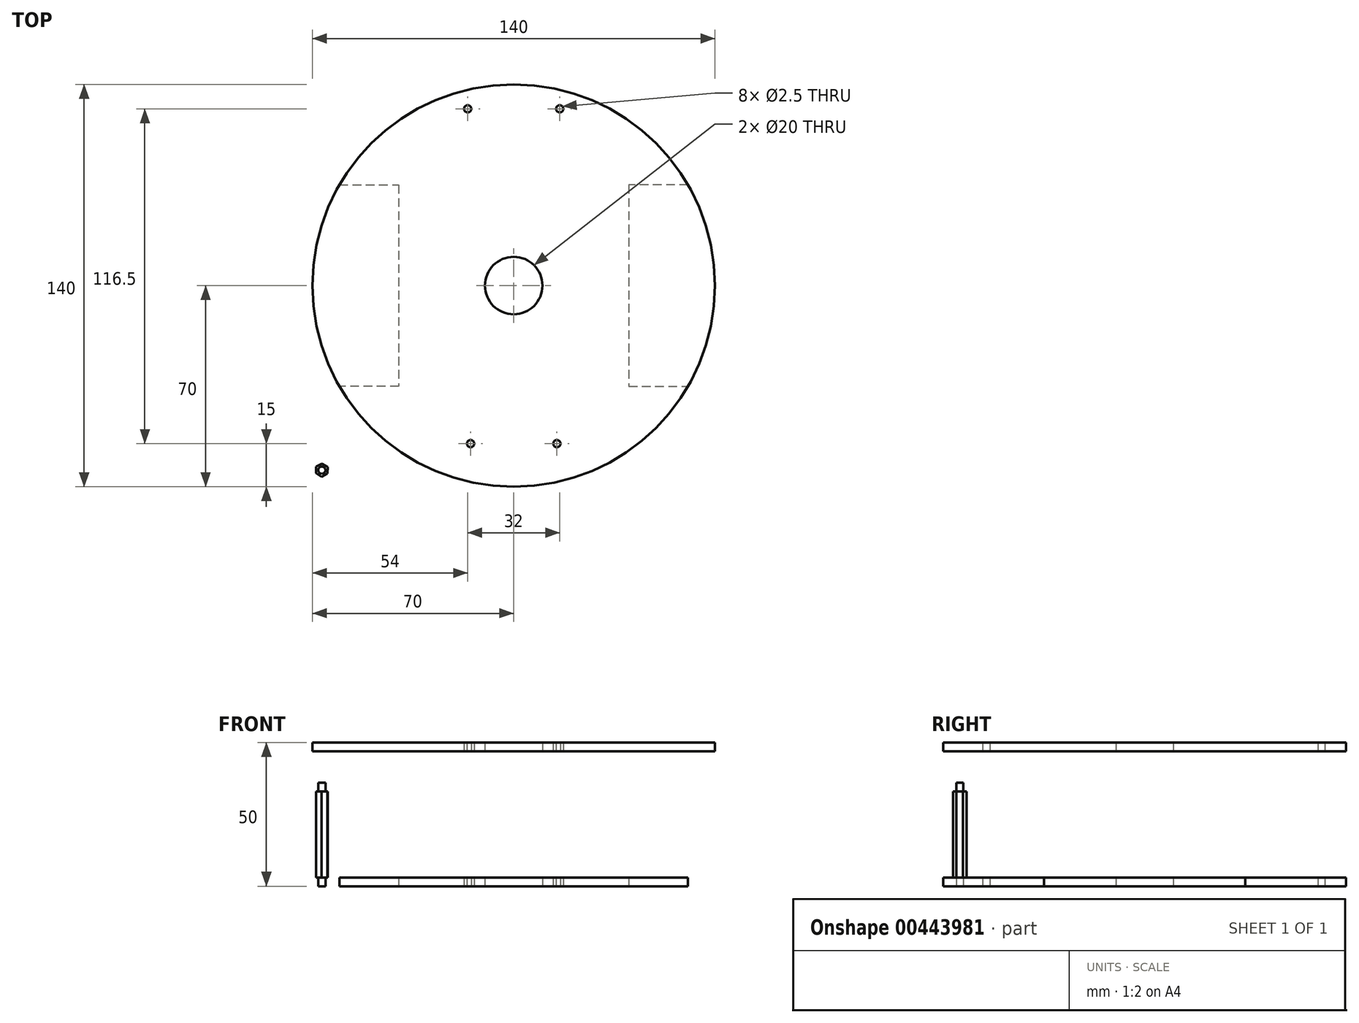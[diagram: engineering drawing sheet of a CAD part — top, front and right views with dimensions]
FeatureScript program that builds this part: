
annotation { "Feature Type Name" : "Feature", "Feature Type Description" : "" }
export const myFeature = defineFeature(function(context is Context, id is Id, definition is map)
    precondition{}
    {
        {
            var Q0;
            Q0=qCreatedBy(makeId("Top.planeOp"),FACE);
            var sketch = newSketch(context, id + "F0", { "sketchPlane" : qUnion([Q0])});
            skCircle(sketch, "E0", {"center": v(0, 0) * mm, "radius": 70 * mm});
            skCircle(sketch, "E1", {"center": v(0, 0) * mm, "radius": 10 * mm});
            skLineSegment(sketch, "E2", {"start": v(-88.17, 35) * mm, "end": v(88.24, 35) * mm, "construction": true});
            skLineSegment(sketch, "E3", {"start": v(88.24, 35) * mm, "end": v(88.24, -35) * mm, "construction": true});
            skLineSegment(sketch, "E4", {"start": v(88.24, -35) * mm, "end": v(-103.41, -35) * mm, "construction": true});
            skLineSegment(sketch, "E5", {"start": v(40, 80.8) * mm, "end": v(40, -81.17) * mm, "construction": true});
            skLineSegment(sketch, "E6", {"start": v(40, -81.17) * mm, "end": v(-40, -81.17) * mm, "construction": true});
            skLineSegment(sketch, "E7", {"start": v(-40, -81.17) * mm, "end": v(-40, 80.41) * mm, "construction": true});
            skLineSegment(sketch, "E8", {"start": v(60.62, 35) * mm, "end": v(40, 35) * mm});
            skLineSegment(sketch, "E9", {"start": v(40, 35) * mm, "end": v(40, -35) * mm});
            skLineSegment(sketch, "E10", {"start": v(40, -35) * mm, "end": v(60.62, -35) * mm});
            skLineSegment(sketch, "E11", {"start": v(-60.62, 35) * mm, "end": v(-40, 35) * mm});
            skLineSegment(sketch, "E12", {"start": v(-40, 35) * mm, "end": v(-40, -35) * mm});
            skLineSegment(sketch, "E13", {"start": v(-40, -35) * mm, "end": v(-60.62, -35) * mm});
            skLineSegment(sketch, "E14", {"start": v(-55.36, 61.5) * mm, "end": v(61.88, 61.5) * mm, "construction": true});
            skLineSegment(sketch, "E15", {"start": v(-62.2, -55) * mm, "end": v(70.52, -55) * mm, "construction": true});
            skCircle(sketch, "E16", {"center": v(-16, 61.5) * mm, "radius": 1.25 * mm});
            skCircle(sketch, "E17.MirrorC", {"center": v(16, 61.5) * mm, "radius": 1.25 * mm});
            skCircle(sketch, "E18.MirrorC", {"center": v(-15, -55) * mm, "radius": 1.25 * mm});
            skCircle(sketch, "E19.MirrorC", {"center": v(15, -55) * mm, "radius": 1.25 * mm});
            skSolve(sketch);
        }
        {
            var Q0;
            Q0=makeQuery(id+"F0.imprint","IMPRINT",FACE,{"disambiguationData":[TD([[makeQuery(id+"F0.imprint","IMPRINT",EDGE,{"derivedFrom":sQuery(id+"F0.wireOp",EDGE,"E1")}),-1.0]])]});
            extrude(context, id + "F1", {"entities" : qUnion([Q0]), "depth" : 3 * mm});
        }
        {
            var Q0;
            {var subQ0=sQuery(id+"F0.wireOp",EDGE,"E11");Q0=makeQuery(id+"F0.imprint","IMPRINT",FACE,{"disambiguationData":[TD([[makeQuery(id+"F0.imprint","IMPRINT",EDGE,{"derivedFrom":subQ0}),-1.0]])]});}
            var Q1;
            Q1=makeQuery(id+"F0.imprint","IMPRINT",FACE,{"disambiguationData":[TD([[makeQuery(id+"F0.imprint","IMPRINT",EDGE,{"derivedFrom":sQuery(id+"F0.wireOp",EDGE,"E1")}),-1.0]])]});
            var Q2;
            {var subQ0=sQuery(id+"F0.wireOp",EDGE,"E8");Q2=makeQuery(id+"F0.imprint","IMPRINT",FACE,{"disambiguationData":[TD([[makeQuery(id+"F0.imprint","IMPRINT",EDGE,{"derivedFrom":subQ0}),1.0]])]});}
            extrude(context, id + "F2", {"entities" : qUnion([Q0, Q1, Q2]), "depth" : 50 * mm, "hasSecondDirection" : true, "secondDirectionOppositeDirection" : false, "secondDirectionDepth" : 47 * mm});
        }
        {
            var Q0;
            Q0=qCreatedBy(makeId("Top.planeOp"),FACE);
            var sketch = newSketch(context, id + "F3", { "sketchPlane" : qUnion([Q0])});
            skCircle(sketch, "E20", {"center": v(-66.72, -64.23) * mm, "radius": 1.25 * mm});
            skSolve(sketch);
        }
        {
            var Q0;
            Q0 = qSketchRegion(id + "F3", true);
            extrude(context, id + "F4", {"entities" : qUnion([Q0]), "depth" : 3 * mm});
        }
        {
            var Q0;
            Q0=makeQuery(id+"F4.opExtrude","CAP_FACE",FACE,{"disambiguationData":[OSD([sQuery(id+"F3.wireOp",EDGE,"E20")])],"isStart":false});
            var sketch = newSketch(context, id + "F5", { "sketchPlane" : qUnion([Q0])});
            skCircle(sketch, "E21.cCircle", {"center": v(-66.72, -64.23) * mm, "radius": 2 * mm, "construction": true});
            skLineSegment(sketch, "E21.0", {"start": v(-64.75, -65.44) * mm, "end": v(-66.78, -66.54) * mm});
            skLineSegment(sketch, "E21.1", {"start": v(-66.78, -66.54) * mm, "end": v(-68.75, -65.33) * mm});
            skLineSegment(sketch, "E21.2", {"start": v(-68.75, -65.33) * mm, "end": v(-68.69, -63.02) * mm});
            skLineSegment(sketch, "E21.3", {"start": v(-68.69, -63.02) * mm, "end": v(-66.66, -61.92) * mm});
            skLineSegment(sketch, "E21.4", {"start": v(-66.66, -61.92) * mm, "end": v(-64.69, -63.13) * mm});
            skLineSegment(sketch, "E21.5", {"start": v(-64.69, -63.13) * mm, "end": v(-64.75, -65.44) * mm});
            skPoint(sketch, "E21.0.midPoint", {"position": v(-65.76, -65.99) * mm});
            skSolve(sketch);
        }
        {
            var Q0;
            Q0 = qSketchRegion(id + "F5", true);
            extrude(context, id + "F6", {"entities" : qUnion([Q0]), "operationType" : NewBodyOperationType.ADD, "depth" : 30 * mm});
        }
        {
            var Q0;
            Q0=makeQuery(id+"F6.opExtrude","CAP_FACE",FACE,{"disambiguationData":[OSD([sQuery(id+"F5.wireOp",EDGE,"E21.0"),sQuery(id+"F5.wireOp",EDGE,"E21.1"),sQuery(id+"F5.wireOp",EDGE,"E21.2"),sQuery(id+"F5.wireOp",EDGE,"E21.3"),sQuery(id+"F5.wireOp",EDGE,"E21.4"),sQuery(id+"F5.wireOp",EDGE,"E21.5")])],"isStart":false});
            var sketch = newSketch(context, id + "F7", { "sketchPlane" : qUnion([Q0])});
            skLineSegment(sketch, "E22", {"start": v(-66.66, -61.92) * mm, "end": v(-66.78, -66.54) * mm, "construction": true});
            skCircle(sketch, "E23", {"center": v(-66.72, -64.23) * mm, "radius": 1.25 * mm});
            skSolve(sketch);
        }
        {
            var Q0;
            Q0=makeQuery(id+"F7.imprint","IMPRINT",FACE,{"disambiguationData":[TD([[makeQuery(id+"F7.imprint","IMPRINT",EDGE,{"derivedFrom":sQuery(id+"F7.wireOp",EDGE,"E23")}),1.0]])]});
            extrude(context, id + "F8", {"entities" : qUnion([Q0]), "operationType" : NewBodyOperationType.ADD, "depth" : 3 * mm});
        }
    });
